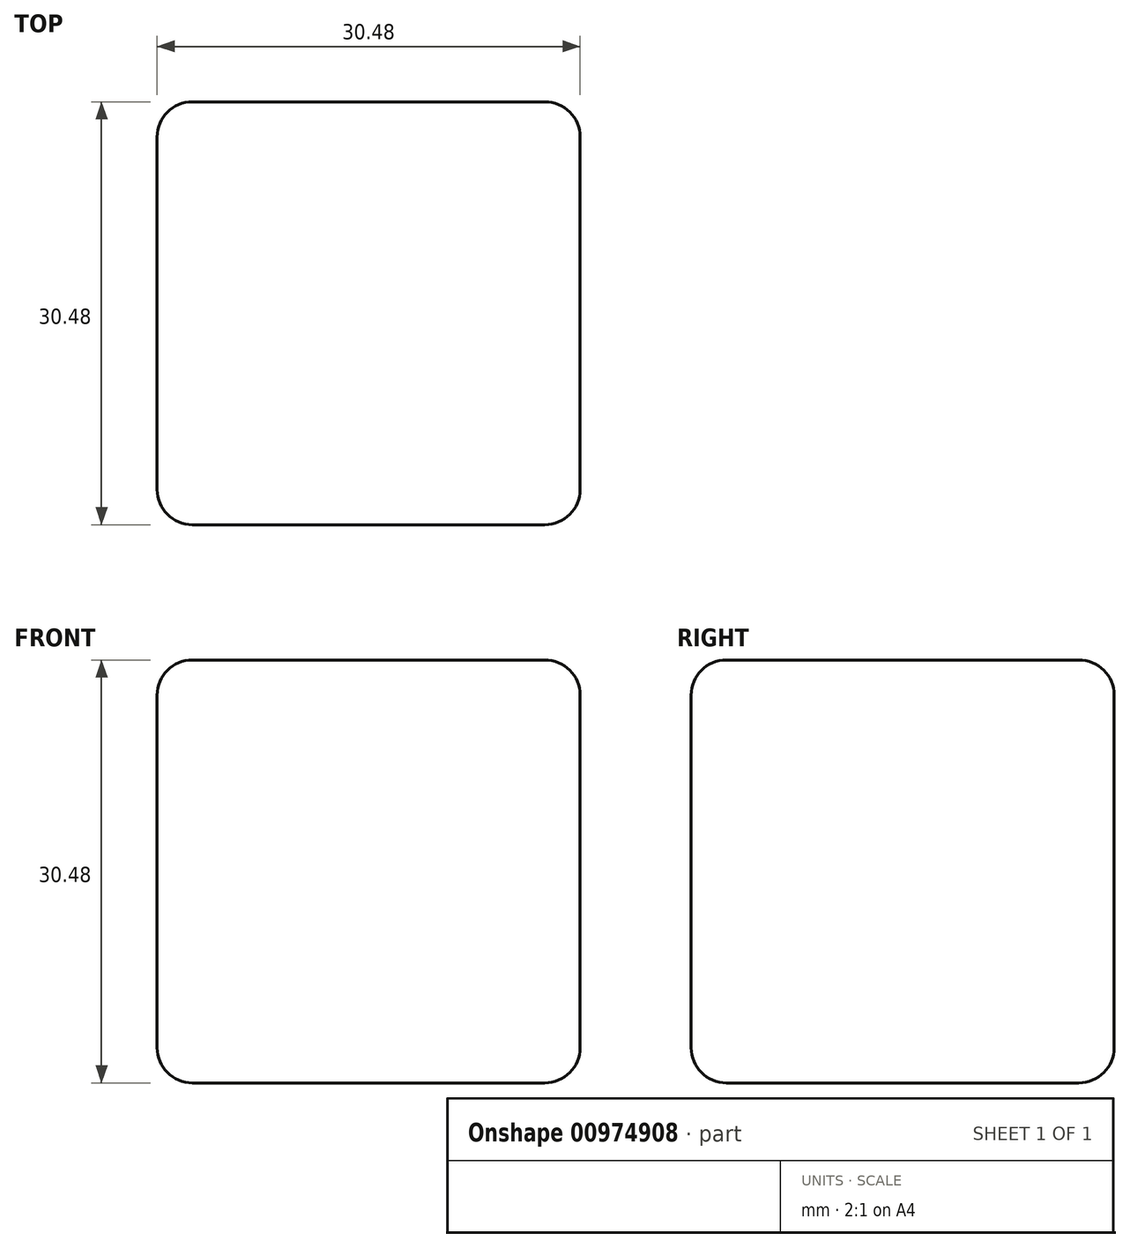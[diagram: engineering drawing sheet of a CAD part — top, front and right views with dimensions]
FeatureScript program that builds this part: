
annotation { "Feature Type Name" : "Feature", "Feature Type Description" : "" }
export const myFeature = defineFeature(function(context is Context, id is Id, definition is map)
    precondition{}
    {
        {
            var Q0;
            Q0=qCreatedBy(makeId("Front.planeOp"),FACE);
            var sketch = newSketch(context, id + "F0", { "sketchPlane" : qUnion([Q0])});
            skLineSegment(sketch, "E0.bottom", {"start": v(15.24, 15.24) * mm, "end": v(-15.24, 15.24) * mm});
            skLineSegment(sketch, "E0.top", {"start": v(15.24, -15.24) * mm, "end": v(-15.24, -15.24) * mm});
            skLineSegment(sketch, "E0.left", {"start": v(15.24, 15.24) * mm, "end": v(15.24, -15.24) * mm});
            skLineSegment(sketch, "E0.right", {"start": v(-15.24, 15.24) * mm, "end": v(-15.24, -15.24) * mm});
            skPoint(sketch, "E0.middle", {"position": v(0, 0) * mm});
            skSolve(sketch);
        }
        {
            var Q0;
            Q0=makeQuery(id+"F0.imprint","IMPRINT",FACE,{"disambiguationData":[TD([[makeQuery(id+"F0.imprint","IMPRINT",EDGE,{"derivedFrom":sQuery(id+"F0.wireOp",EDGE,"E0.bottom")}),1.0]])]});
            extrude(context, id + "F1", {"entities" : qUnion([Q0]), "endBound" : BoundingType.SYMMETRIC, "depth" : 30.48 * mm, "offsetDistance" : 25.4 * mm});
        }
        {
            var Q0;
            Q0=makeQuery(id+"F1.opExtrude","CAP_EDGE",EDGE,{"disambiguationData":[OSD([sQuery(id+"F0.wireOp",EDGE,"E0.left")])],"isStart":false});
            var Q1;
            Q1=makeQuery(id+"F1.opExtrude","SWEPT_EDGE",EDGE,{"disambiguationData":[OSD([sQuery(id+"F0.wireOp",EDGE,"E0.bottom"),sQuery(id+"F0.wireOp",EDGE,"E0.left")])]});
            var Q2;
            Q2=makeQuery(id+"F1.opExtrude","CAP_EDGE",EDGE,{"disambiguationData":[OSD([sQuery(id+"F0.wireOp",EDGE,"E0.left")])],"isStart":true});
            var Q3;
            Q3=makeQuery(id+"F1.opExtrude","SWEPT_EDGE",EDGE,{"disambiguationData":[OSD([sQuery(id+"F0.wireOp",EDGE,"E0.top"),sQuery(id+"F0.wireOp",EDGE,"E0.left")])]});
            var Q4;
            Q4=makeQuery(id+"F1.opExtrude","SWEPT_FACE",FACE,{"disambiguationData":[OSD([sQuery(id+"F0.wireOp",EDGE,"E0.top")])]});
            var Q5;
            Q5=makeQuery(id+"F1.opExtrude","CAP_EDGE",EDGE,{"disambiguationData":[OSD([sQuery(id+"F0.wireOp",EDGE,"E0.bottom")])],"isStart":false});
            var Q6;
            Q6=makeQuery(id+"F1.opExtrude","CAP_EDGE",EDGE,{"disambiguationData":[OSD([sQuery(id+"F0.wireOp",EDGE,"E0.right")])],"isStart":false});
            var Q7;
            Q7=makeQuery(id+"F1.opExtrude","SWEPT_EDGE",EDGE,{"disambiguationData":[OSD([sQuery(id+"F0.wireOp",EDGE,"E0.bottom"),sQuery(id+"F0.wireOp",EDGE,"E0.right")])]});
            var Q8;
            Q8=makeQuery(id+"F1.opExtrude","CAP_EDGE",EDGE,{"disambiguationData":[OSD([sQuery(id+"F0.wireOp",EDGE,"E0.bottom")])],"isStart":true});
            var Q9;
            Q9=makeQuery(id+"F1.opExtrude","CAP_EDGE",EDGE,{"disambiguationData":[OSD([sQuery(id+"F0.wireOp",EDGE,"E0.right")])],"isStart":true});
            fillet(context, id + "F2", {"entities" : qUnion([Q0, Q1, Q2, Q3, Q4, Q5, Q6, Q7, Q8, Q9]), "radius" : 2.54 * mm, "tangentPropagation" : true, "allowEdgeOverflow" : false});
        }
    });
